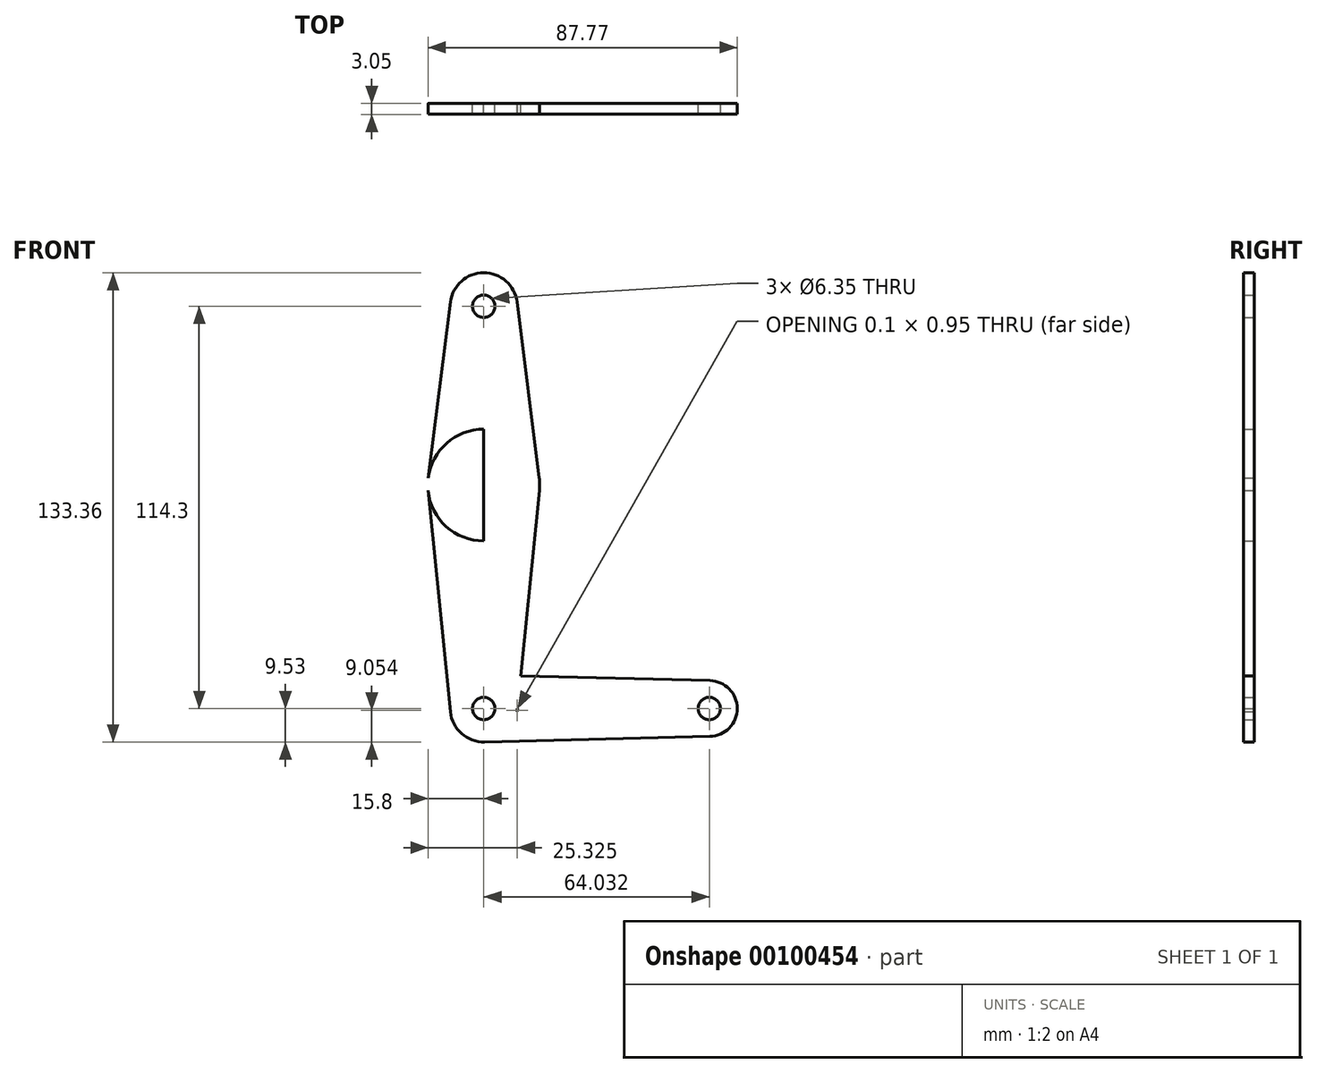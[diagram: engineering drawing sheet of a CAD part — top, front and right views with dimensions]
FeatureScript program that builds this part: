
annotation { "Feature Type Name" : "Feature", "Feature Type Description" : "" }
export const myFeature = defineFeature(function(context is Context, id is Id, definition is map)
    precondition{}
    {
        {
            var Q0;
            Q0=qCreatedBy(makeId("Front.planeOp"),FACE);
            var sketch = newSketch(context, id + "F0", { "sketchPlane" : qUnion([Q0])});
            skLineSegment(sketch, "E0", {"start": v(0, 114.3) * mm, "end": v(0, 0) * mm});
            skLineSegment(sketch, "E1", {"start": v(0, 0) * mm, "end": v(64.03, 0) * mm});
            skCircle(sketch, "E2", {"center": v(0, 114.3) * mm, "radius": 9.53 * mm});
            skCircle(sketch, "E3", {"center": v(0, 63.5) * mm, "radius": 15.88 * mm});
            skCircle(sketch, "E4", {"center": v(0, 0) * mm, "radius": 9.53 * mm});
            skCircle(sketch, "E5", {"center": v(64.03, 0) * mm, "radius": 7.94 * mm});
            skLineSegment(sketch, "E6", {"start": v(-9.45, 115.5) * mm, "end": v(-15.75, 65.48) * mm});
            skLineSegment(sketch, "E7", {"start": v(9.45, 115.5) * mm, "end": v(15.75, 65.48) * mm});
            skLineSegment(sketch, "E8", {"start": v(-15.8, 61.91) * mm, "end": v(-9.48, -0.95) * mm});
            skLineSegment(sketch, "E9", {"start": v(15.8, 61.91) * mm, "end": v(9.48, -0.95) * mm});
            skLineSegment(sketch, "E10", {"start": v(0.24, 9.52) * mm, "end": v(64.23, 7.94) * mm});
            skLineSegment(sketch, "E11", {"start": v(0.24, -9.52) * mm, "end": v(64.23, -7.94) * mm});
            skCircle(sketch, "E12", {"center": v(0, 114.3) * mm, "radius": 3.18 * mm});
            skCircle(sketch, "E13", {"center": v(0, 0) * mm, "radius": 3.18 * mm});
            skCircle(sketch, "E14", {"center": v(64.03, 0) * mm, "radius": 3.18 * mm});
            skSolve(sketch);
        }
        {
            var Q0;
            {var subQ5=sQuery(id+"F0.wireOp",EDGE,"E6");Q0=makeQuery(id+"F0.imprint","IMPRINT",FACE,{"disambiguationData":[TD([[makeQuery(id+"F0.imprint","IMPRINT",EDGE,{"derivedFrom":subQ5}),1.0]])]});}
            var Q1;
            {var subQ5=sQuery(id+"F0.wireOp",EDGE,"E7");Q1=makeQuery(id+"F0.imprint","IMPRINT",FACE,{"disambiguationData":[TD([[makeQuery(id+"F0.imprint","IMPRINT",EDGE,{"derivedFrom":subQ5}),-1.0]])]});}
            var Q2;
            {var subQ0=sQuery(id+"F0.wireOp",EDGE,"E3");var subQ1=sQuery(id+"F0.wireOp",EDGE,"E0");var subQ2=makeQuery(id+"F0.imprint","INTERSECT",VERTEX,{"disambiguationData":[OD(0.0)],"derivedFrom":[subQ1,subQ0]});Q2=makeQuery(id+"F0.imprint","IMPRINT",FACE,{"disambiguationData":[TD([[makeQuery(id+"F0.imprint","IMPRINT",EDGE,{"disambiguationData":[TD([[subQ2,-1.0]])],"derivedFrom":subQ1}),1.0]])]});}
            var Q3;
            {var subQ0=sQuery(id+"F0.wireOp",EDGE,"E3");var subQ1=sQuery(id+"F0.wireOp",EDGE,"E0");var subQ2=makeQuery(id+"F0.imprint","INTERSECT",VERTEX,{"disambiguationData":[OD(0.0)],"derivedFrom":[subQ1,subQ0]});Q3=makeQuery(id+"F0.imprint","IMPRINT",FACE,{"disambiguationData":[TD([[makeQuery(id+"F0.imprint","IMPRINT",EDGE,{"disambiguationData":[TD([[subQ2,-1.0]])],"derivedFrom":subQ1}),-1.0]])]});}
            var Q4;
            {var subQ5=sQuery(id+"F0.wireOp",EDGE,"E8");Q4=makeQuery(id+"F0.imprint","IMPRINT",FACE,{"disambiguationData":[TD([[makeQuery(id+"F0.imprint","IMPRINT",EDGE,{"derivedFrom":subQ5}),1.0]])]});}
            var Q5;
            Q5=makeQuery(id+"F0.imprint","IMPRINT",FACE,{"disambiguationData":[TD([[makeQuery(id+"F0.imprint","IMPRINT",EDGE,{"derivedFrom":sQuery(id+"F0.wireOp",EDGE,"E12")}),-1.0]])]});
            var Q6;
            Q6=makeQuery(id+"F0.imprint","IMPRINT",FACE,{"disambiguationData":[TD([[makeQuery(id+"F0.imprint","IMPRINT",EDGE,{"derivedFrom":sQuery(id+"F0.wireOp",EDGE,"E14")}),-1.0]])]});
            var Q7;
            {var subQ1=sQuery(id+"F0.wireOp",EDGE,"E3");var subQ7=sQuery(id+"F0.wireOp",EDGE,"E0");var subQ9=makeQuery(id+"F0.imprint","INTERSECT",VERTEX,{"disambiguationData":[OD(1.0)],"derivedFrom":[subQ7,subQ1]});Q7=makeQuery(id+"F0.imprint","IMPRINT",FACE,{"disambiguationData":[TD([[makeQuery(id+"F0.imprint","IMPRINT",EDGE,{"disambiguationData":[TD([[subQ9,-1.0]])],"derivedFrom":subQ7}),1.0]])]});}
            var Q8;
            {var subQ0=sQuery(id+"F0.wireOp",EDGE,"E4");var subQ1=sQuery(id+"F0.wireOp",EDGE,"E1");var subQ2=makeQuery(id+"F0.imprint","INTERSECT",VERTEX,{"derivedFrom":[subQ1,subQ0]});Q8=makeQuery(id+"F0.imprint","IMPRINT",FACE,{"disambiguationData":[TD([[makeQuery(id+"F0.imprint","IMPRINT",EDGE,{"disambiguationData":[TD([[subQ2,-1.0]])],"derivedFrom":subQ1}),1.0]])]});}
            var Q9;
            {var subQ7=sQuery(id+"F0.wireOp",EDGE,"E11");Q9=makeQuery(id+"F0.imprint","IMPRINT",FACE,{"disambiguationData":[TD([[makeQuery(id+"F0.imprint","IMPRINT",EDGE,{"derivedFrom":subQ7}),1.0]])]});}
            var Q10;
            {var subQ0=sQuery(id+"F0.wireOp",EDGE,"E4");var subQ3=sQuery(id+"F0.wireOp",EDGE,"E0");var subQ4=makeQuery(id+"F0.imprint","INTERSECT",VERTEX,{"derivedFrom":[subQ3,subQ0]});Q10=makeQuery(id+"F0.imprint","IMPRINT",FACE,{"disambiguationData":[TD([[makeQuery(id+"F0.imprint","IMPRINT",EDGE,{"disambiguationData":[TD([[subQ4,-1.0]])],"derivedFrom":subQ3}),-1.0]])]});}
            var Q11;
            {var subQ0=sQuery(id+"F0.wireOp",EDGE,"E4");var subQ2=sQuery(id+"F0.wireOp",EDGE,"E0");var subQ3=makeQuery(id+"F0.imprint","INTERSECT",VERTEX,{"derivedFrom":[subQ2,subQ0]});Q11=makeQuery(id+"F0.imprint","IMPRINT",FACE,{"disambiguationData":[TD([[makeQuery(id+"F0.imprint","IMPRINT",EDGE,{"disambiguationData":[TD([[subQ3,-1.0]])],"derivedFrom":subQ2}),1.0]])]});}
            var Q12;
            {var subQ0=sQuery(id+"F0.wireOp",EDGE,"E5");var subQ1=sQuery(id+"F0.wireOp",EDGE,"E1");var subQ2=makeQuery(id+"F0.imprint","INTERSECT",VERTEX,{"derivedFrom":[subQ1,subQ0]});Q12=makeQuery(id+"F0.imprint","IMPRINT",FACE,{"disambiguationData":[TD([[makeQuery(id+"F0.imprint","IMPRINT",EDGE,{"disambiguationData":[TD([[subQ2,1.0]])],"derivedFrom":subQ1}),1.0]])]});}
            extrude(context, id + "F1", {"entities" : qUnion([Q0, Q1, Q2, Q3, Q4, Q5, Q6, Q7, Q8, Q9, Q10, Q11, Q12]), "depth" : 3.05 * mm});
        }
    });
